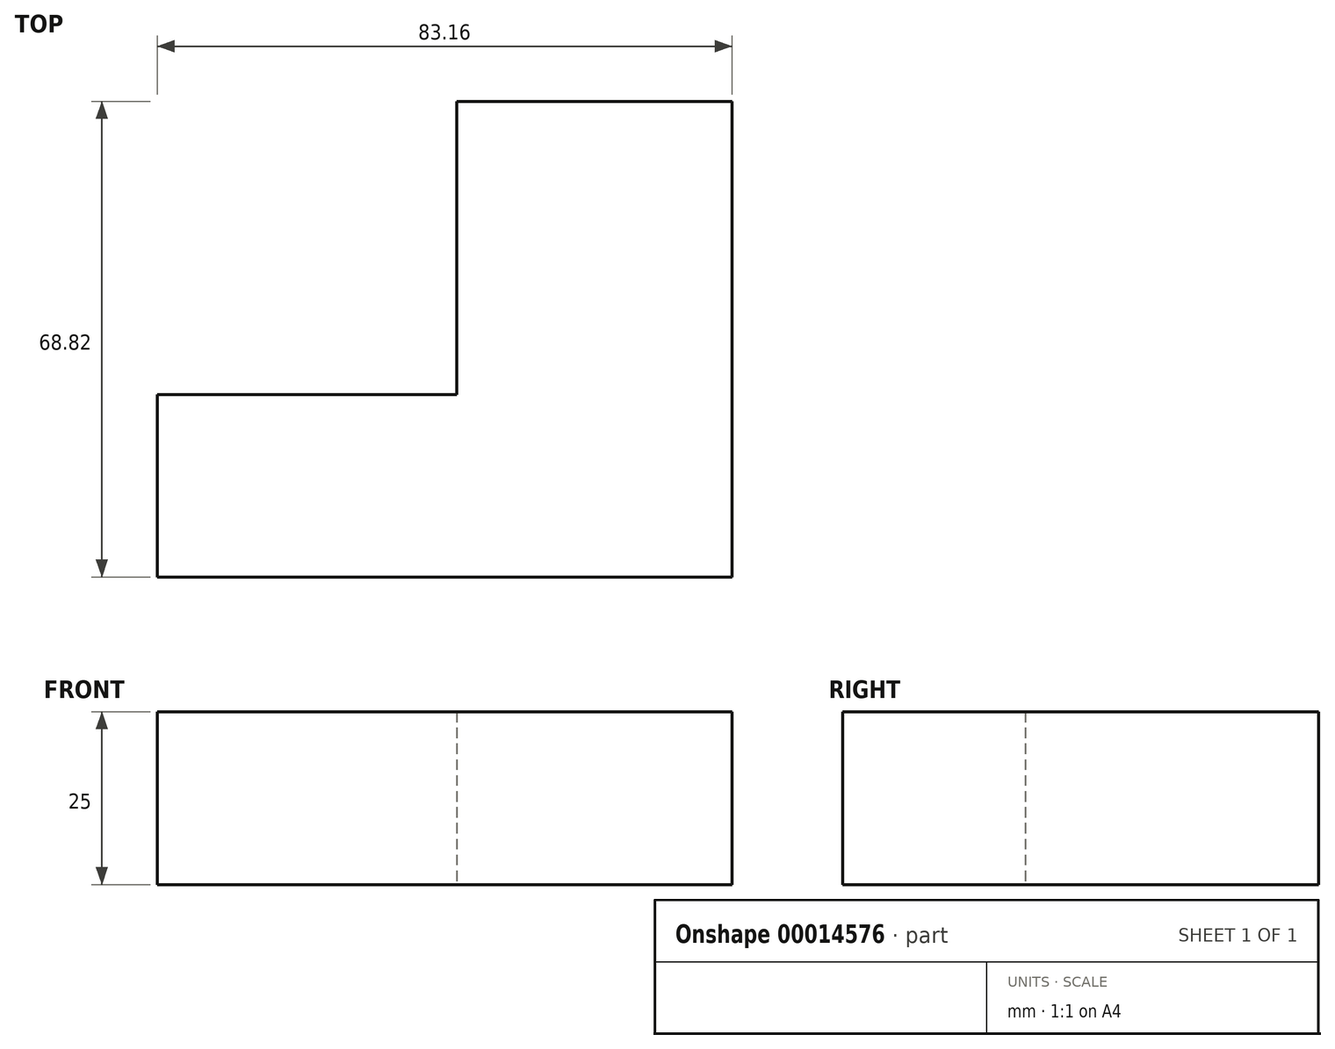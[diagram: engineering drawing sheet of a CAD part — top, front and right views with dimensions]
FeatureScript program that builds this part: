
annotation { "Feature Type Name" : "Feature", "Feature Type Description" : "" }
export const myFeature = defineFeature(function(context is Context, id is Id, definition is map)
    precondition{}
    {
        {
            var Q0;
            Q0=qCreatedBy(makeId("Top.planeOp"),FACE);
            var sketch = newSketch(context, id + "F0", { "sketchPlane" : qUnion([Q0])});
            skLineSegment(sketch, "E0.bottom", {"start": v(-43.3, -23.37) * mm, "end": v(39.85, -23.37) * mm});
            skLineSegment(sketch, "E0.top", {"start": v(-43.3, -49.8) * mm, "end": v(39.85, -49.8) * mm});
            skLineSegment(sketch, "E0.left", {"start": v(-43.3, -23.37) * mm, "end": v(-43.3, -49.8) * mm});
            skLineSegment(sketch, "E0.right", {"start": v(39.85, -23.37) * mm, "end": v(39.85, -49.8) * mm});
            skLineSegment(sketch, "E1.bottom", {"start": v(39.85, -49.8) * mm, "end": v(0, -49.8) * mm});
            skLineSegment(sketch, "E1.top", {"start": v(39.85, 19.03) * mm, "end": v(0, 19.03) * mm});
            skLineSegment(sketch, "E1.left", {"start": v(39.85, -49.8) * mm, "end": v(39.85, 19.03) * mm});
            skLineSegment(sketch, "E1.right", {"start": v(0, -49.8) * mm, "end": v(0, 19.03) * mm});
            skSolve(sketch);
        }
        {
            var Q0;
            {var subQ4=sQuery(id+"F0.wireOp",EDGE,"E0.top");Q0=makeQuery(id+"F0.imprint","IMPRINT",FACE,{"disambiguationData":[TD([[makeQuery(id+"F0.imprint","IMPRINT",EDGE,{"derivedFrom":subQ4}),1.0]])]});}
            var Q1;
            {var subQ5=sQuery(id+"F0.wireOp",EDGE,"E1.top");Q1=makeQuery(id+"F0.imprint","IMPRINT",FACE,{"disambiguationData":[TD([[makeQuery(id+"F0.imprint","IMPRINT",EDGE,{"derivedFrom":subQ5}),1.0]])]});}
            var Q2;
            {var subQ5=sQuery(id+"F0.wireOp",EDGE,"E1.bottom");Q2=makeQuery(id+"F0.imprint","IMPRINT",FACE,{"disambiguationData":[TD([[makeQuery(id+"F0.imprint","IMPRINT",EDGE,{"derivedFrom":subQ5}),-1.0]])]});}
            var Q3;
            Q3=makeQuery(id+"FTgcYzdnx24hmogUC_0.imprint","IMPRINT",FACE,{"disambiguationData":[TD([[makeQuery(id+"FTgcYzdnx24hmogUC_0.imprint","IMPRINT",EDGE,{"derivedFrom":sQuery(id+"FTgcYzdnx24hmogUC_0.wireOp",EDGE,"5741c229-95ac-4a3b-9951-abd32dfddcd7.bottom")}),-1.0]])]});
            extrude(context, id + "F1", {"entities" : qUnion([Q0, Q1, Q2, Q3]), "depth" : 25 * mm});
        }
    });
